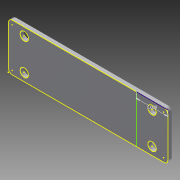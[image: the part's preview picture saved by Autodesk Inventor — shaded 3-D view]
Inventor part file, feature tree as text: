
AUTODESK INVENTOR PART (.ipt)
format: ipt  version: 2013 (Build 170138000, 138)  size: 110,592 bytes
history: native  units: in
note: dims shown in document units (in); Inventor stores cm internally (conversion verified against a paired STEP export)
features: sketch x3, extrude x2, fillet x1
ambient origin geometry x8: Origin, YZ Plane, XZ Plane, XY Plane, X Axis, Y Axis, Z Axis, Center Point
bodies: Solid1 (feature_tree)
feature tree (6):
  extrude  "Extrusion1"  Depth=5.046in
  extrude  "Extrusion2"  Depth=0.5in
  fillet  "Fillet1"  Radius=0.25in
  sketch  "Sketch3"  dims[d6=1.0in d7=0.266in d8=0.266in d9=0.5in d10=0.25in d11=0.266in d12=0.266in d13=1.0in d14=0.125in d15=0.0in d16=0.125in d17=1.0in]
  sketch  "Sketch1"  dims[d0=1.5in d1=5.046in]
  sketch  "Sketch2"  dims[d2=0.125in d3=0.0in d4=0.5in d5=0.25in]
